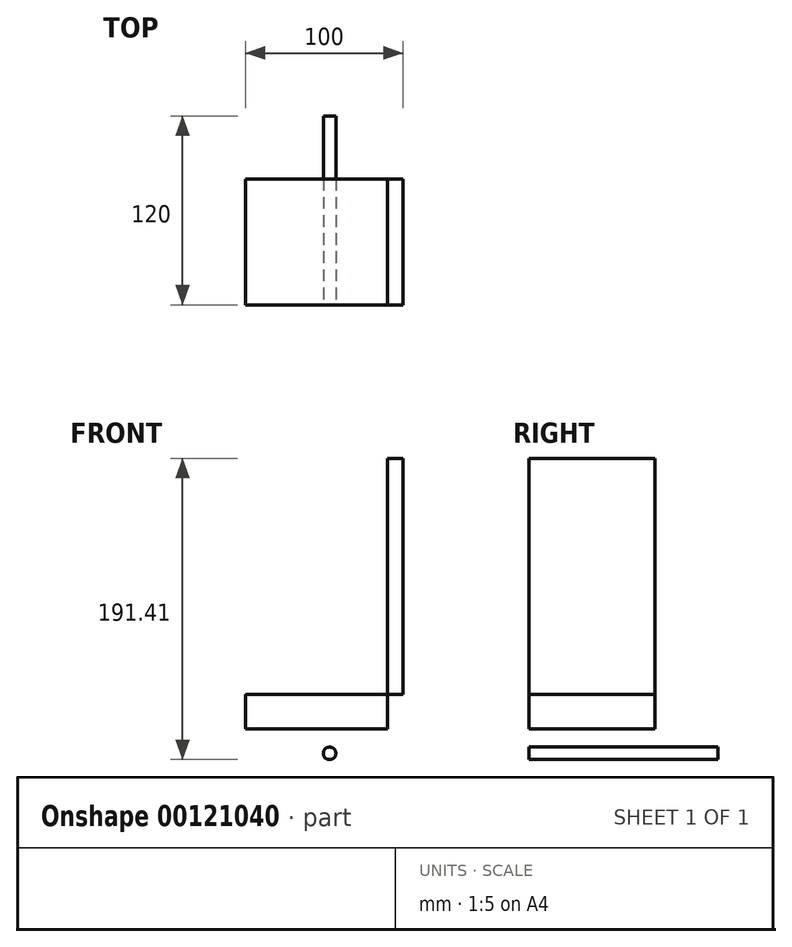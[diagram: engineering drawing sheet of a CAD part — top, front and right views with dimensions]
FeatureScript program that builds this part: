
annotation { "Feature Type Name" : "Feature", "Feature Type Description" : "" }
export const myFeature = defineFeature(function(context is Context, id is Id, definition is map)
    precondition{}
    {
        {
            var Q0;
            Q0=qCreatedBy(makeId("Top.planeOp"),FACE);
            var sketch = newSketch(context, id + "F0", { "sketchPlane" : qUnion([Q0])});
            skLineSegment(sketch, "E0.bottom", {"start": v(0, 0) * mm, "end": v(90, 0) * mm});
            skLineSegment(sketch, "E0.top", {"start": v(0, 80) * mm, "end": v(90, 80) * mm});
            skLineSegment(sketch, "E0.left", {"start": v(0, 0) * mm, "end": v(0, 80) * mm});
            skLineSegment(sketch, "E0.right", {"start": v(90, 0) * mm, "end": v(90, 80) * mm});
            skSolve(sketch);
        }
        {
            var Q0;
            Q0 = qSketchRegion(id + "F0", true);
            extrude(context, id + "F1", {"entities" : qUnion([Q0]), "depth" : 22 * mm});
        }
        {
            var Q0;
            Q0=qCreatedBy(makeId("Front.planeOp"),FACE);
            var sketch = newSketch(context, id + "F2", { "sketchPlane" : qUnion([Q0])});
            skCircle(sketch, "E1", {"center": v(53.37, -15.4) * mm, "radius": 4 * mm});
            skSolve(sketch);
        }
        {
            var Q0;
            Q0 = qSketchRegion(id + "F2", true);
            extrude(context, id + "F3", {"entities" : qUnion([Q0]), "oppositeDirection" : true, "depth" : 120 * mm});
        }
        {
            var Q0;
            Q0=makeQuery(id+"F1.opExtrude","SWEPT_FACE",FACE,{"disambiguationData":[OSD([sQuery(id+"F0.wireOp",EDGE,"E0.right")])]});
            var sketch = newSketch(context, id + "F4", { "sketchPlane" : qUnion([Q0])});
            skLineSegment(sketch, "E2", {"start": v(0, 22) * mm, "end": v(80, 22) * mm});
            skLineSegment(sketch, "E3", {"start": v(40, 22) * mm, "end": v(40, 0) * mm, "construction": true});
            skLineSegment(sketch, "E4", {"start": v(0, 22) * mm, "end": v(0, 172) * mm});
            skLineSegment(sketch, "E5", {"start": v(0, 172) * mm, "end": v(80, 172) * mm});
            skLineSegment(sketch, "E6", {"start": v(80, 172) * mm, "end": v(80, 22) * mm});
            skSolve(sketch);
        }
        {
            var Q0;
            Q0 = qSketchRegion(id + "F4", true);
            extrude(context, id + "F5", {"entities" : qUnion([Q0]), "depth" : 10 * mm});
        }
    });
